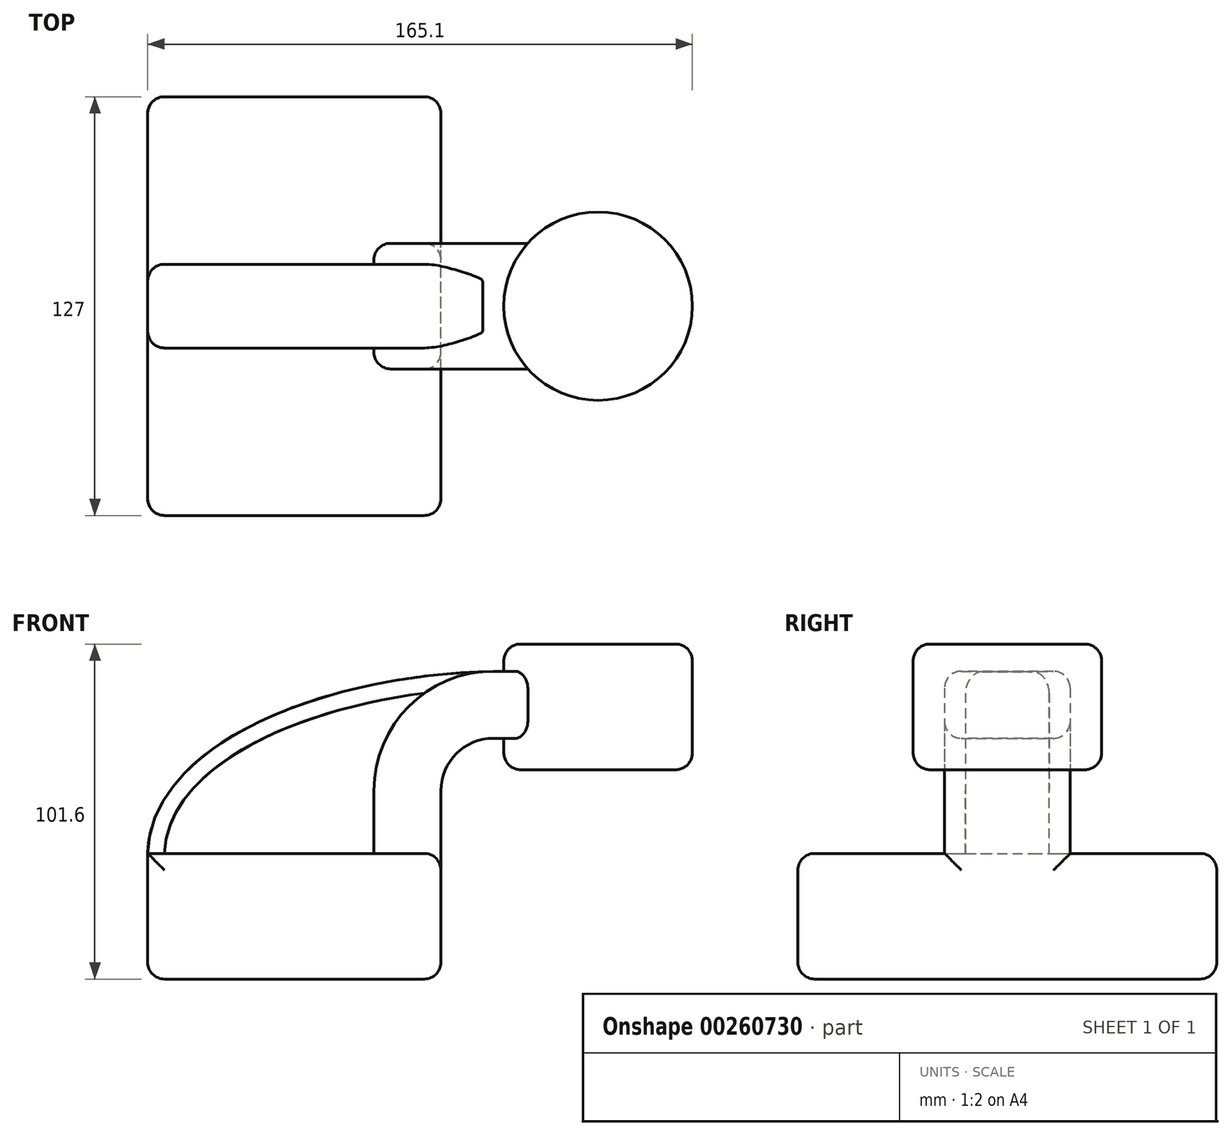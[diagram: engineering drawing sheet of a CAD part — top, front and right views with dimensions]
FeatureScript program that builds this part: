
annotation { "Feature Type Name" : "Feature", "Feature Type Description" : "" }
export const myFeature = defineFeature(function(context is Context, id is Id, definition is map)
    precondition{}
    {
        {
            var Q0;
            Q0=qCreatedBy(makeId("Front.planeOp"),FACE);
            var sketch = newSketch(context, id + "F0", { "sketchPlane" : qUnion([Q0])});
            skLineSegment(sketch, "E0.bottom", {"start": v(44.45, -19.05) * mm, "end": v(-44.45, -19.05) * mm});
            skLineSegment(sketch, "E0.top", {"start": v(44.45, 19.05) * mm, "end": v(-44.45, 19.05) * mm});
            skLineSegment(sketch, "E0.left", {"start": v(44.45, -19.05) * mm, "end": v(44.45, 19.05) * mm});
            skLineSegment(sketch, "E0.right", {"start": v(-44.45, -19.05) * mm, "end": v(-44.45, 19.05) * mm});
            skPoint(sketch, "E0.middle", {"position": v(0, 0) * mm});
            skLineSegment(sketch, "E1.bottom", {"start": v(120.65, 44.45) * mm, "end": v(57.15, 44.45) * mm});
            skLineSegment(sketch, "E1.top", {"start": v(120.65, 82.55) * mm, "end": v(57.15, 82.55) * mm});
            skLineSegment(sketch, "E1.left", {"start": v(120.65, 44.45) * mm, "end": v(120.65, 82.55) * mm});
            skLineSegment(sketch, "E1.right", {"start": v(57.15, 44.45) * mm, "end": v(57.15, 82.55) * mm});
            skPoint(sketch, "E1.middle", {"position": v(88.9, 63.5) * mm});
            skLineSegment(sketch, "E2", {"start": v(51.86, 44.45) * mm, "end": v(57.15, 44.45) * mm});
            skLineSegment(sketch, "E3", {"start": v(44.45, 19.05) * mm, "end": v(44.45, 38.1) * mm});
            skArc(sketch, "E4", {"start": v(44.45, 38.1) * mm, "mid": v(49.1, 49.33) * mm, "end": v(60.32, 53.98) * mm});
            skLineSegment(sketch, "E5", {"start": v(60.32, 53.98) * mm, "end": v(92.07, 53.98) * mm});
            skLineSegment(sketch, "E6.0", {"start": v(60.32, 74.3) * mm, "end": v(92.07, 74.3) * mm});
            skArc(sketch, "E6.1", {"start": v(24.13, 38.1) * mm, "mid": v(34.73, 63.7) * mm, "end": v(60.32, 74.3) * mm});
            skLineSegment(sketch, "E6.2", {"start": v(24.13, 19.05) * mm, "end": v(24.13, 38.1) * mm});
            skFitSpline(sketch, "E7", {"points": [v(-44.45, 19.05) * mm, v(57.15, 74.16) * mm], "startDerivative": vector(2.74, 100.12) * mm, "endDerivative": vector(145.79, 4.62) * mm});
            skLineSegment(sketch, "E8", {"start": v(92.07, 44.45) * mm, "end": v(92.07, 82.55) * mm});
            skPoint(sketch, "E8.startSnap0", {"position": v(88.9, 44.45) * mm});
            skSolve(sketch);
        }
        {
            var Q0;
            Q0=makeQuery(id+"F0.imprint","IMPRINT",FACE,{"disambiguationData":[TD([[makeQuery(id+"F0.imprint","IMPRINT",EDGE,{"derivedFrom":sQuery(id+"F0.wireOp",EDGE,"E0.bottom")}),-1.0]])]});
            extrude(context, id + "F1", {"entities" : qUnion([Q0]), "endBound" : BoundingType.SYMMETRIC, "depth" : 127 * mm});
        }
        {
            var Q0;
            {var subQ2=sQuery(id+"F0.wireOp",EDGE,"E6.2");Q0=makeQuery(id+"F0.imprint","IMPRINT",FACE,{"disambiguationData":[TD([[makeQuery(id+"F0.imprint","IMPRINT",EDGE,{"derivedFrom":subQ2}),1.0]])]});}
            extrude(context, id + "F2", {"entities" : qUnion([Q0]), "operationType" : NewBodyOperationType.ADD, "endBound" : BoundingType.SYMMETRIC, "depth" : 25.4 * mm});
        }
        {
            var Q0;
            {var subQ1=sQuery(id+"F0.wireOp",EDGE,"E3");Q0=makeQuery(id+"F0.imprint","IMPRINT",FACE,{"disambiguationData":[TD([[makeQuery(id+"F0.imprint","IMPRINT",EDGE,{"derivedFrom":subQ1}),1.0]])]});}
            var Q1;
            {var subQ1=sQuery(id+"F0.wireOp",EDGE,"E5");Q1=makeQuery(id+"F0.imprint","IMPRINT",FACE,{"disambiguationData":[TD([[makeQuery(id+"F0.imprint","IMPRINT",EDGE,{"derivedFrom":subQ1}),1.0]])]});}
            extrude(context, id + "F3", {"entities" : qUnion([Q0, Q1]), "operationType" : NewBodyOperationType.ADD, "endBound" : BoundingType.SYMMETRIC, "depth" : 38.1 * mm});
        }
        {
            var Q0;
            {var subQ0=sQuery(id+"F0.wireOp",EDGE,"E1.left");Q0=makeQuery(id+"F0.imprint","IMPRINT",FACE,{"disambiguationData":[TD([[makeQuery(id+"F0.imprint","IMPRINT",EDGE,{"derivedFrom":subQ0}),1.0]])]});}
            var Q1;
            Q1=sQuery(id+"F0.wireOp",EDGE,"E8");
            revolve(context, id + "F4", {"operationType" : NewBodyOperationType.ADD, "entities" : qUnion([Q0]), "axis" : qUnion([Q1]), "revolveType" : RevolveType.FULL});
        }
        {
            var Q0;
            Q0=makeQuery(id+"F1.opExtrude","CAP_FACE",FACE,{"disambiguationData":[OSD([sQuery(id+"F0.wireOp",EDGE,"E0.bottom"),sQuery(id+"F0.wireOp",EDGE,"E0.top"),sQuery(id+"F0.wireOp",EDGE,"E0.left"),sQuery(id+"F0.wireOp",EDGE,"E0.right")])],"isStart":false});
            var Q1;
            Q1=makeQuery(id+"F3.boolean.opBoolean","MERGE",FACE,{"derivedFrom":[makeQuery(id+"F1.opExtrude","SWEPT_FACE",FACE,{"disambiguationData":[OSD([sQuery(id+"F0.wireOp",EDGE,"E0.left")])]}),makeQuery(id+"F3.opExtrude","SWEPT_FACE",FACE,{"disambiguationData":[OSD([sQuery(id+"F0.wireOp",EDGE,"E3")])]})]});
            var Q2;
            Q2=makeQuery(id+"F1.opExtrude","CAP_FACE",FACE,{"disambiguationData":[OSD([sQuery(id+"F0.wireOp",EDGE,"E0.bottom"),sQuery(id+"F0.wireOp",EDGE,"E0.top"),sQuery(id+"F0.wireOp",EDGE,"E0.left"),sQuery(id+"F0.wireOp",EDGE,"E0.right")])],"isStart":true});
            fillet(context, id + "F5", {"entities" : qUnion([Q0, Q1, Q2]), "radius" : 5.08 * mm, "tangentPropagation" : true, "allowEdgeOverflow" : false});
        }
        {
            var Q0;
            Q0=makeQuery(id+"F2.opExtrude","CAP_EDGE",EDGE,{"disambiguationData":[OSD([sQuery(id+"F0.wireOp",EDGE,"E7")])],"isStart":false});
            var Q1;
            Q1=makeQuery(id+"F2.opExtrude","CAP_EDGE",EDGE,{"disambiguationData":[OSD([sQuery(id+"F0.wireOp",EDGE,"E7")])],"isStart":true});
            var Q2;
            Q2=makeQuery(id+"F4.opRevolve","SWEPT_EDGE",EDGE,{"disambiguationData":[OSD([sQuery(id+"F0.wireOp",EDGE,"E1.bottom"),sQuery(id+"F0.wireOp",EDGE,"E1.left")])]});
            var Q3;
            Q3=makeQuery(id+"F4.opRevolve","SWEPT_EDGE",EDGE,{"disambiguationData":[OSD([sQuery(id+"F0.wireOp",EDGE,"E1.top"),sQuery(id+"F0.wireOp",EDGE,"E1.left")])]});
            var Q4;
            Q4=makeQuery(id+"F3.opExtrude","CAP_EDGE",EDGE,{"disambiguationData":[OSD([sQuery(id+"F0.wireOp",EDGE,"E6.1")])],"isStart":false});
            var Q5;
            Q5=makeQuery(id+"F3.opExtrude","CAP_EDGE",EDGE,{"disambiguationData":[OSD([sQuery(id+"F0.wireOp",EDGE,"E6.1")])],"isStart":true});
            var Q6;
            Q6=makeQuery(id+"F1.opExtrude","SWEPT_EDGE",EDGE,{"disambiguationData":[OSD([sQuery(id+"F0.wireOp",EDGE,"E0.bottom"),sQuery(id+"F0.wireOp",EDGE,"E0.right")])]});
            fillet(context, id + "F6", {"entities" : qUnion([Q0, Q1, Q2, Q3, Q4, Q5, Q6]), "radius" : 5.08 * mm, "tangentPropagation" : true, "allowEdgeOverflow" : false});
        }
    });
